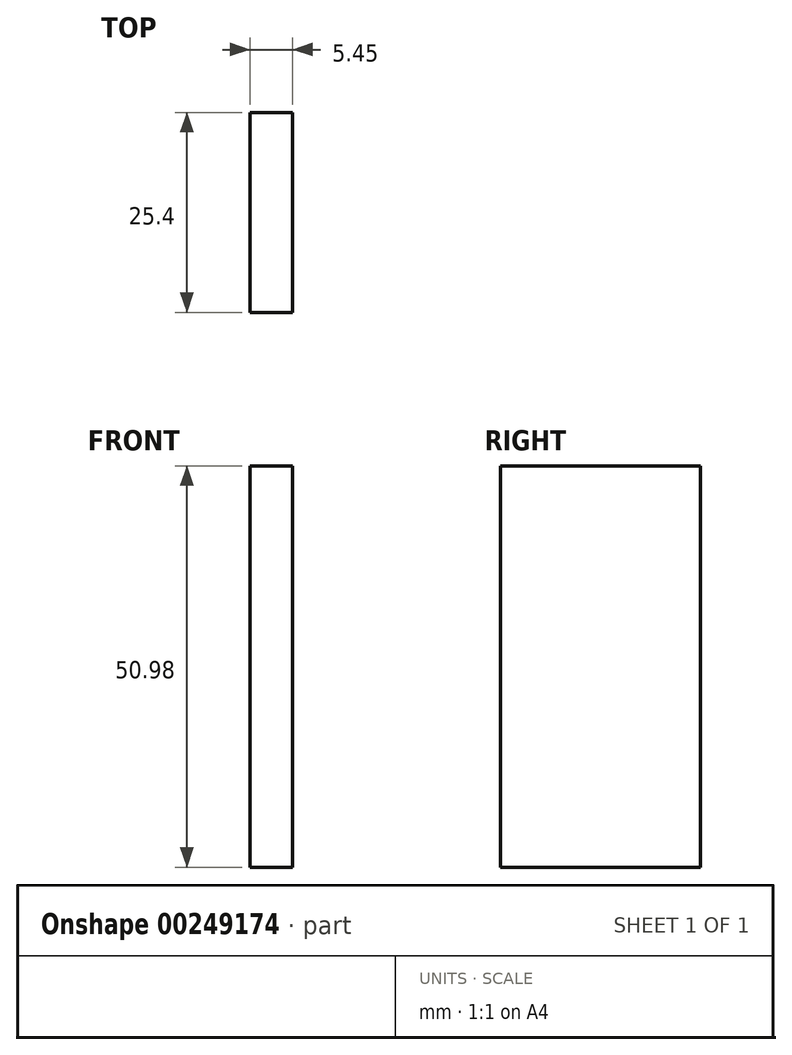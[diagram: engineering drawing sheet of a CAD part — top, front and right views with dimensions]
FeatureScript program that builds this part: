
annotation { "Feature Type Name" : "Feature", "Feature Type Description" : "" }
export const myFeature = defineFeature(function(context is Context, id is Id, definition is map)
    precondition{}
    {
        {
            var Q0;
            Q0=qCreatedBy(makeId("Front.planeOp"),FACE);
            var sketch = newSketch(context, id + "F0", { "sketchPlane" : qUnion([Q0])});
            skLineSegment(sketch, "E0.bottom", {"start": v(0, 0) * mm, "end": v(5.45, 0) * mm});
            skLineSegment(sketch, "E0.top", {"start": v(0, 50.98) * mm, "end": v(5.45, 50.98) * mm});
            skLineSegment(sketch, "E0.left", {"start": v(0, 0) * mm, "end": v(0, 50.98) * mm});
            skLineSegment(sketch, "E0.right", {"start": v(5.45, 0) * mm, "end": v(5.45, 50.98) * mm});
            skSolve(sketch);
        }
        {
            var Q0;
            Q0 = qSketchRegion(id + "F0", true);
            extrude(context, id + "F1", {"entities" : qUnion([Q0]), "depth" : 25.4 * mm});
        }
    });
